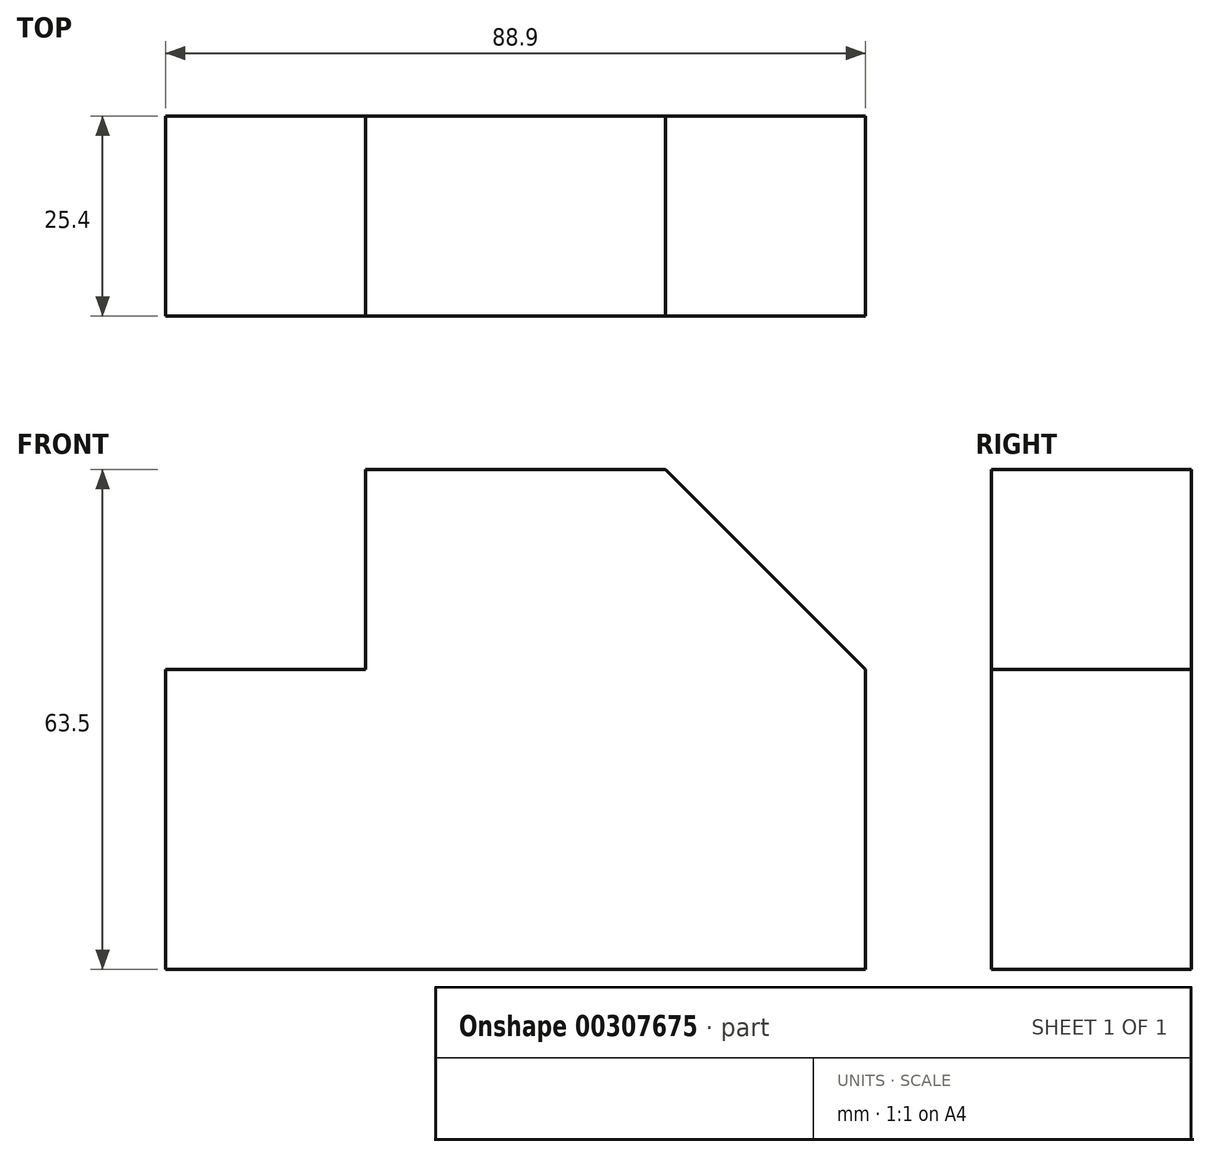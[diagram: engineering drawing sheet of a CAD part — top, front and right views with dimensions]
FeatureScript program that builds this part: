
annotation { "Feature Type Name" : "Feature", "Feature Type Description" : "" }
export const myFeature = defineFeature(function(context is Context, id is Id, definition is map)
    precondition{}
    {
        {
            var Q0;
            Q0=qCreatedBy(makeId("Front.planeOp"),FACE);
            var sketch = newSketch(context, id + "F0", { "sketchPlane" : qUnion([Q0])});
            skLineSegment(sketch, "E0", {"start": v(27.66, -38.24) * mm, "end": v(-61.24, -38.24) * mm});
            skLineSegment(sketch, "E1", {"start": v(-61.24, -38.24) * mm, "end": v(-61.24, -0.14) * mm});
            skLineSegment(sketch, "E2", {"start": v(-61.24, -0.14) * mm, "end": v(-35.84, -0.14) * mm});
            skLineSegment(sketch, "E3", {"start": v(-35.84, -0.14) * mm, "end": v(-35.84, 25.26) * mm});
            skLineSegment(sketch, "E4", {"start": v(-35.84, 25.26) * mm, "end": v(2.26, 25.26) * mm});
            skLineSegment(sketch, "E5", {"start": v(2.26, 25.26) * mm, "end": v(27.66, -0.14) * mm});
            skLineSegment(sketch, "E6", {"start": v(27.66, -0.14) * mm, "end": v(27.66, -38.24) * mm});
            skSolve(sketch);
        }
        {
            var Q0;
            Q0=makeQuery(id+"F0.imprint","IMPRINT",FACE,{"disambiguationData":[TD([[makeQuery(id+"F0.imprint","IMPRINT",EDGE,{"derivedFrom":sQuery(id+"F0.wireOp",EDGE,"E0")}),-1.0]])]});
            extrude(context, id + "F1", {"entities" : qUnion([Q0]), "depth" : 25.4 * mm});
        }
    });
